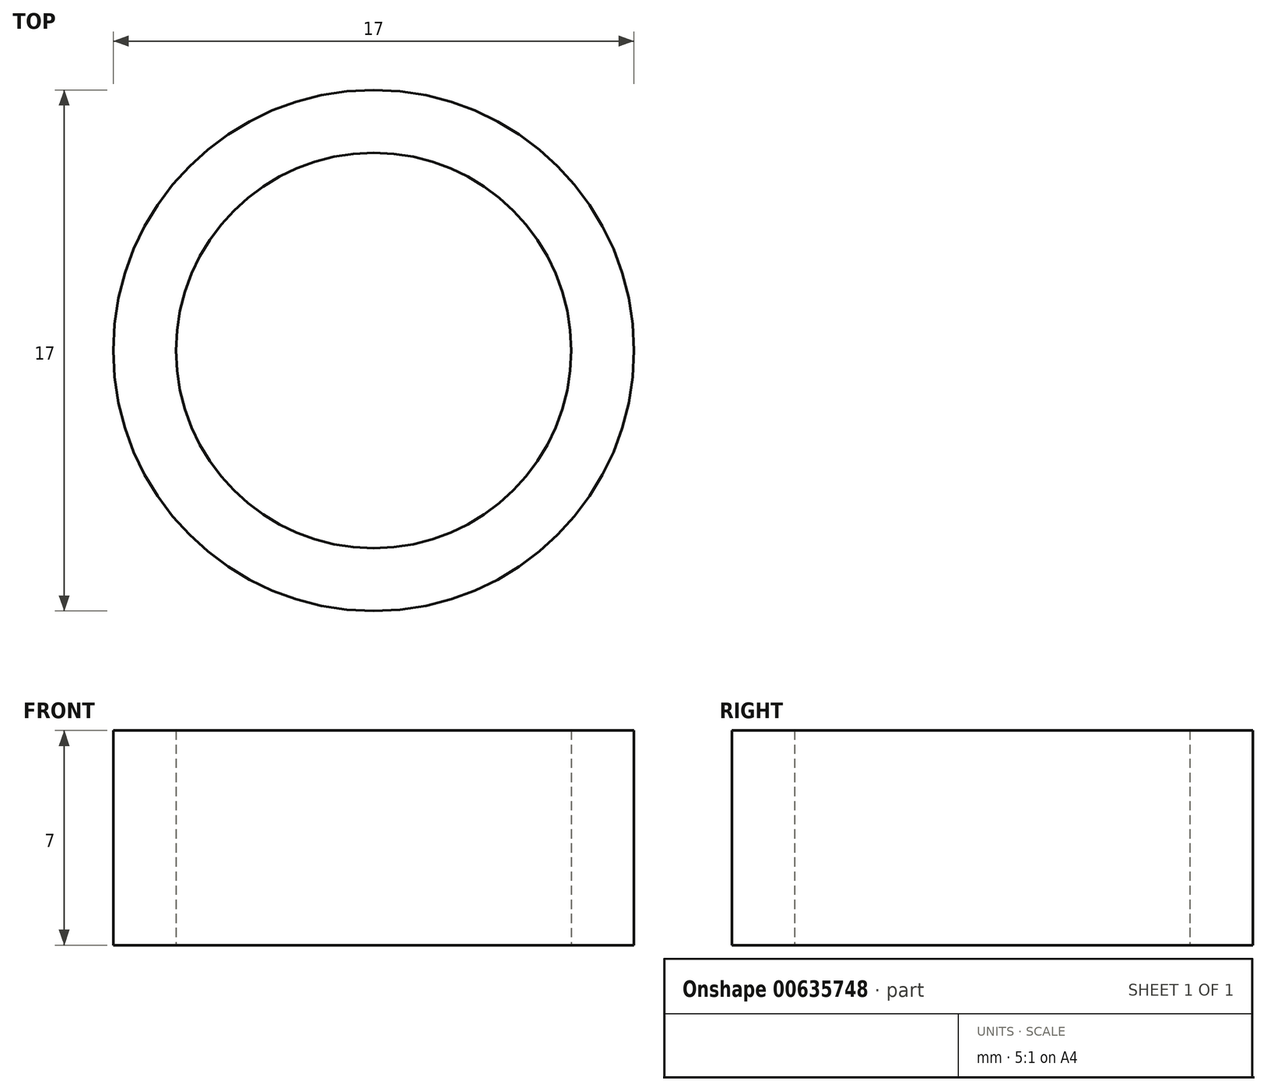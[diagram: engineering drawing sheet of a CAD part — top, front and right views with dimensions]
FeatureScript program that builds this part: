
annotation { "Feature Type Name" : "Feature", "Feature Type Description" : "" }
export const myFeature = defineFeature(function(context is Context, id is Id, definition is map)
    precondition{}
    {
        {
            var Q0;
            Q0=qCreatedBy(makeId("Top.planeOp"),FACE);
            var sketch = newSketch(context, id + "F0", { "sketchPlane" : qUnion([Q0])});
            skCircle(sketch, "E0", {"center": v(0, 0) * mm, "radius": 6.45 * mm});
            skCircle(sketch, "E1", {"center": v(0, 0) * mm, "radius": 8.5 * mm});
            skSolve(sketch);
        }
        {
            var Q0;
            Q0=makeQuery(id+"F0.imprint","IMPRINT",FACE,{"disambiguationData":[TD([[makeQuery(id+"F0.imprint","IMPRINT",EDGE,{"derivedFrom":sQuery(id+"F0.wireOp",EDGE,"E0")}),-1.0]])]});
            extrude(context, id + "F1", {"entities" : qUnion([Q0]), "depth" : 7 * mm, "offsetDistance" : 25 * mm});
        }
    });
